# Revit family: PRD_AR_WllMntdBbTps_WallOutlet_ACXX1010
name_source: partatom
category: Plumbing Fixtures
units: mm (PartAtom-declared; Revit-internal decimal feet)

## family parameters
Cut with Voids When Loaded = No
Enable Cutting in Views = Yes
Host = Face
Maintain Annotation Orientation = No
OmniClass Number = 23.45.55.14
OmniClass Title = Single Faucets
Part Type = Normal
Room Calculation Point = No
Round Connector Dimension = Use Diameter
Shared = No

## types (1)
- ACXX1010
    Angle = 45
    AssetType = Fixed
    BIMObjectName = PRD_AR_WallMountedBibTaps_WallOutlet_ACXX1010
    BodyMaterial = PRD_AR_StainlessSteel_Brushed
    CW Connection = Yes
    CWFU = 0
    Category = Pr_40_20_87_93, Wall-mounted bib taps
    CloseOffRating = 0.0 Pa
    Default Elevation = 1219 mm
    Description = Wall outlet DN 15 for mounting on in-wall washbasin taps.Especially suitable for facilities at risk of vandalism. Suicide-proofhousing with anti-twist protection, moulded rosette, anti-theftaerator with integrated flow regulator 5.7 l/min, SLIM design, tiltangle 45°C, projection 69 mm, brushed stainless steel with mountingmaterial.
    Export Type to IFC As = IfcValveType
    FaucetFunction = Mixed
    FaucetOperation = OTHER
    FaucetType = OTHER
    Features = Wall outlet DN 15 for mounting on in-wall washbasin taps.
    Finish = Brushed stainless steel
    Flow = 0.1 L/s
    FlowCoefficient = 0.1
    HW Connection = Yes
    HWFU = 0
    IfcExportAs = IfcValveType
    IfcExportType = FAUCET
    Manufacturer = KWC Group Management AG
    ManufacturerName = KWC Group Management AG
    ManufacturerURL = www.kwc-professional.com
    Material = brushed stainless steel
    Model = ACXX1010
    ModelNumber = 2030071663
    ModelReference = ACXX1010
    NBSDescription = Taps and water supply fittings for sinks
    NBSReference = 45-35-70/345
    Name = Wall Outlet ACXX1010
    NominalDepth = 0 mm  [stored 0 ft]
    NominalHeight = 0 mm  [stored 0 ft]
    NominalWidth = 55 mm  [stored 0.180446 ft]
    OverallWidth = 55 mm
    ProductInformation = http://pim.kwc.com
    Quantity = 1
    QuantityUom = Piece
    Size = 15
    SpoutProjection = 70 mm
    Status = New
    TestPressure = 0.0 Pa
    Type IFC Predefined Type = FAUCET
    TypeOfSpout = Wall outlet
    URL = www.kwc-professional.com
    Uniclass2015Code = Pr_40_20_87_93
    Uniclass2015Title = Wall-mounted bib taps
    Uniclass2015Version = Products v1.36
    ValveMechanism = OTHER
    ValveOperation = OTHER
    ValvePattern = OTHER
    Vent Connection = Yes
    Version = 1
    VolumeFlowRateAt3Bar = 0.1 l/s
    WFU = 0
    Waste Connection = Yes
    WorkingPressure = 0.0 Pa

note: [stored X ft] marks values corroborated as IEEE doubles in the binary element streams (Revit-internal decimal feet)

## geometry (parser evidence)
native form markers: Sweep x5
no freeform markers — native parametric forms only
